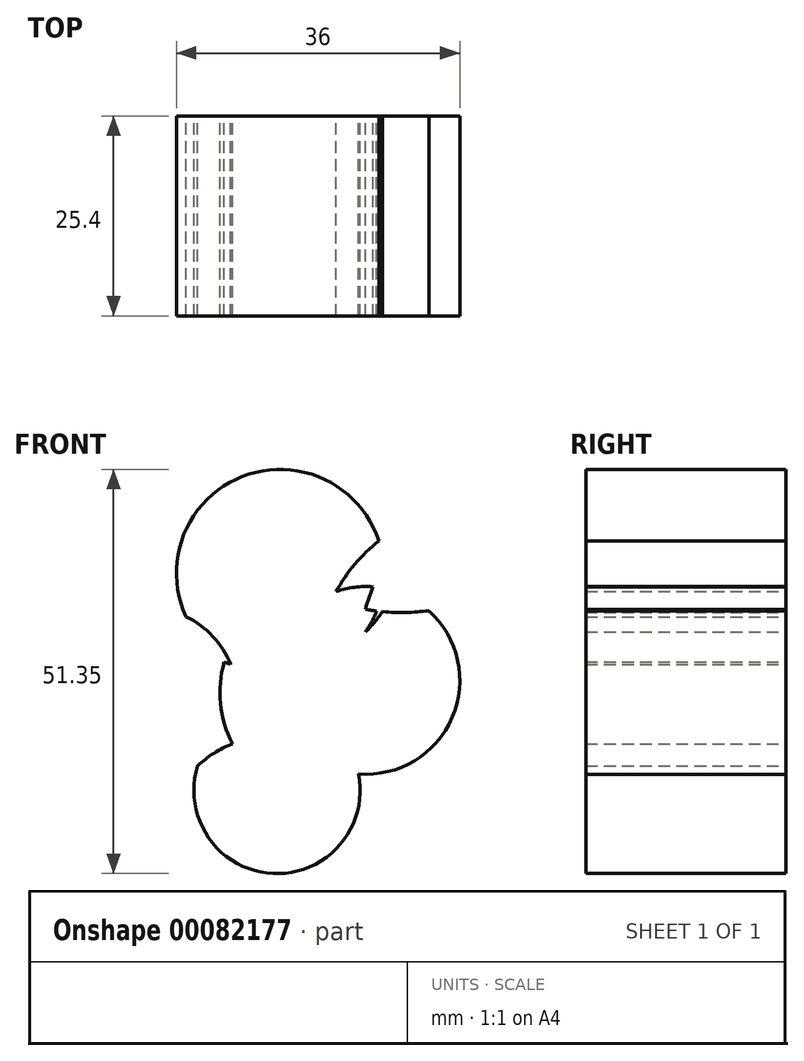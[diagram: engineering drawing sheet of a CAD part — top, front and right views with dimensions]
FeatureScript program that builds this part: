
annotation { "Feature Type Name" : "Feature", "Feature Type Description" : "" }
export const myFeature = defineFeature(function(context is Context, id is Id, definition is map)
    precondition{}
    {
        {
            var Q0;
            Q0=qCreatedBy(makeId("Front.planeOp"),FACE);
            var sketch = newSketch(context, id + "F0", { "sketchPlane" : qUnion([Q0])});
            skArc(sketch, "E0", {"start": v(-49.95, 30.35) * mm, "mid": v(-65.58, 1.37) * mm, "end": v(-33.1, 6.82) * mm});
            skArc(sketch, "E1", {"start": v(-22.94, 40.51) * mm, "mid": v(-46.57, 62.32) * mm, "end": v(-49.95, 30.35) * mm});
            skArc(sketch, "E2", {"start": v(-3.78, 25.41) * mm, "mid": v(2.65, 53.29) * mm, "end": v(-22.94, 40.51) * mm});
            skArc(sketch, "E3", {"start": v(2.9, 0) * mm, "mid": v(19, 17.81) * mm, "end": v(-3.78, 25.41) * mm});
            skArc(sketch, "E4", {"start": v(-15.4, -12.63) * mm, "mid": v(15.25, -37.45) * mm, "end": v(2.9, 0) * mm});
            skArc(sketch, "E5", {"start": v(-33.1, 6.82) * mm, "mid": v(-60.7, -36.09) * mm, "end": v(-15.4, -12.63) * mm});
            skArc(sketch, "E6", {"start": v(2.9, 0) * mm, "mid": v(46.56, 25.06) * mm, "end": v(-3.78, 25.41) * mm});
            skArc(sketch, "E7", {"start": v(-3.78, 25.41) * mm, "mid": v(16.88, 71.34) * mm, "end": v(-22.94, 40.51) * mm});
            skArc(sketch, "E8", {"start": v(-22.94, 40.51) * mm, "mid": v(-51.08, 74.31) * mm, "end": v(-49.95, 30.35) * mm});
            skArc(sketch, "E9", {"start": v(-49.95, 30.35) * mm, "mid": v(-79.98, -8.94) * mm, "end": v(-33.1, 6.82) * mm});
            skArc(sketch, "E10", {"start": v(-15.4, -12.63) * mm, "mid": v(20.81, -45.5) * mm, "end": v(2.9, 0) * mm});
            skArc(sketch, "E11", {"start": v(-33.1, 6.82) * mm, "mid": v(-46.7, -23.35) * mm, "end": v(-15.4, -12.63) * mm});
            skArc(sketch, "E12", {"start": v(-3.78, 22.5) * mm, "mid": v(-19.7, 51.37) * mm, "end": v(-20.91, 18.43) * mm});
            skArc(sketch, "E13", {"start": v(-15.74, 34.73) * mm, "mid": v(-35.72, 55.02) * mm, "end": v(-49.95, 30.35) * mm});
            skArc(sketch, "E14", {"start": v(-28.66, 23.53) * mm, "mid": v(-55.88, 21.84) * mm, "end": v(-33.1, 6.82) * mm});
            skArc(sketch, "E15", {"start": v(0, 0) * mm, "mid": v(28.11, 29.03) * mm, "end": v(-9.87, 15.25) * mm});
            skArc(sketch, "E16", {"start": v(-33.37, -11.2) * mm, "mid": v(-8.23, -30.79) * mm, "end": v(0, 0) * mm});
            skArc(sketch, "E17", {"start": v(-20.04, 8.57) * mm, "mid": v(-19.02, -18.73) * mm, "end": v(-4.65, 4.5) * mm});
            skArc(sketch, "E18", {"start": v(-20.91, 18.43) * mm, "mid": v(-40.96, 20.25) * mm, "end": v(-30.5, 3.05) * mm});
            skArc(sketch, "E19", {"start": v(-25.1, 5.52) * mm, "mid": v(-15.53, -8.15) * mm, "end": v(-4.65, 4.5) * mm});
            skArc(sketch, "E20", {"start": v(-4.65, 4.5) * mm, "mid": v(4.24, 25.28) * mm, "end": v(-15.4, 14.09) * mm});
            skArc(sketch, "E21", {"start": v(-3.78, 22.5) * mm, "mid": v(-17.65, 42.83) * mm, "end": v(-20.91, 18.44) * mm});
            skArc(sketch, "E22", {"start": v(-14.81, 27.44) * mm, "mid": v(-22.25, 14.98) * mm, "end": v(-15, 2.4) * mm});
            skSolve(sketch);
        }
        {
            var Q0;
            {var subQ21=sQuery(id+"F0.wireOp",EDGE,"E19");Q0=makeQuery(id+"F0.imprint","IMPRINT",FACE,{"disambiguationData":[TD([[makeQuery(id+"F0.imprint","IMPRINT",EDGE,{"derivedFrom":subQ21}),1.0]])]});}
            extrude(context, id + "F1", {"entities" : qUnion([Q0]), "depth" : 25.4 * mm});
        }
    });
